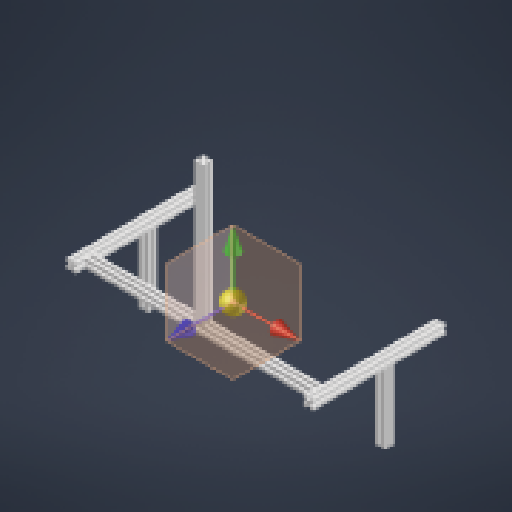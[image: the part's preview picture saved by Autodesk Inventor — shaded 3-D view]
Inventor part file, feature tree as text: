
AUTODESK INVENTOR PART (.ipt)
format: ipt  version: 2024 (Build 280153000, 153)  size: 472,064 bytes
history: native  units: mm
features: projected_geometry x12, extrude x6, sketch x6, reference x5, other x4
ambient origin geometry x8: Origin, YZ Plane, XZ Plane, XY Plane, X Axis, Y Axis, Z Axis, Center Point
bodies: Body1 (feature_tree)
feature tree (33):
  other  "솔리드1"
  extrude  "돌출1"  Depth=20.0mm
  extrude  "돌출2"  Depth=20.0mm
  extrude  "돌출3"  Depth=5.5mm
  extrude  "돌출4"  Depth=5.5mm
  extrude  "돌출5"  Depth=5.5mm
  extrude  "돌출6"  Depth=5.5mm
  sketch  "스케치1"
  reference  "참조1"
  sketch  "스케치2"
  projected_geometry  "투영된 루프1"
  projected_geometry  "투영된 루프2"
  sketch  "스케치3"
  projected_geometry  "투영된 루프3"
  projected_geometry  "투영된 루프4"
  reference  "참조2"
  reference  "참조3"
  sketch  "스케치4"
  projected_geometry  "투영된 루프5"
  projected_geometry  "투영된 루프6"
  projected_geometry  "투영된 루프7"
  projected_geometry  "투영된 루프8"
  projected_geometry  "투영된 루프9"
  reference  "참조4"
  reference  "참조5"
  sketch  "스케치5"
  projected_geometry  "투영된 루프10"
  projected_geometry  "투영된 루프11"
  sketch  "스케치6"
  projected_geometry  "투영된 루프12"
  other  "<userpath>\OneDrive\AAST\PART\ABCD\ABCD Assemble.iam"
  other  "ABCD Assemble.iam"
  other  "acrillboard:1"
